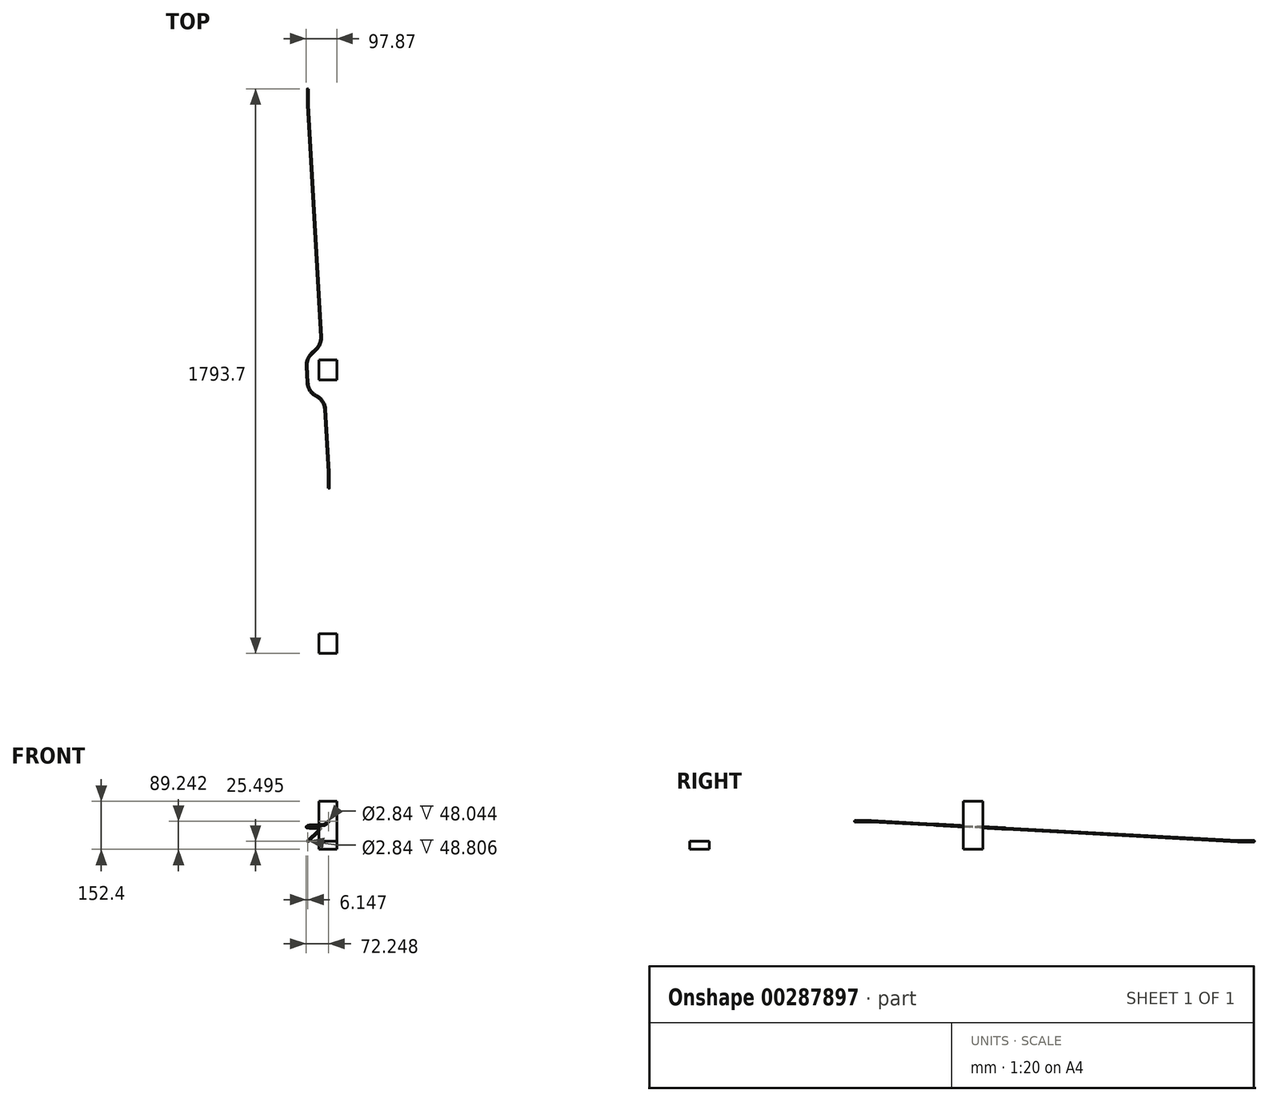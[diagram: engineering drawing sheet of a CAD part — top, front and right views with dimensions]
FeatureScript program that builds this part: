
annotation { "Feature Type Name" : "Feature", "Feature Type Description" : "" }
export const myFeature = defineFeature(function(context is Context, id is Id, definition is map)
    precondition{}
    {
        {
            var Q0;
            Q0=qCreatedBy(makeId("Top.planeOp"),FACE);
            var sketch = newSketch(context, id + "F0", { "sketchPlane" : qUnion([Q0])});
            skLineSegment(sketch, "E0", {"start": v(0, 0) * mm, "end": v(2.87, 0) * mm});
            skLineSegment(sketch, "E1", {"start": v(2.87, 0) * mm, "end": v(2.87, 58) * mm});
            skLineSegment(sketch, "E2", {"start": v(2.87, 58) * mm, "end": v(28.27, 58) * mm});
            skLineSegment(sketch, "E3", {"start": v(0, 0) * mm, "end": v(-63.23, 0) * mm});
            skLineSegment(sketch, "E4", {"start": v(-63.23, 0) * mm, "end": v(-63.23, 1327.37) * mm});
            skLineSegment(sketch, "E5", {"start": v(-63.23, 1327.37) * mm, "end": v(-37.83, 1327.37) * mm});
            skSolve(sketch);
        }
        {
            var Q0;
            Q0=sQuery(id+"F0.wireOp",EDGE,"E5");
            cPlane(context, id + "F1", {"entities" : qUnion([Q0]), "cplaneType" : CPlaneType.LINE_ANGLE, "offset" : 25.4 * mm, "angle" : 0 * degree, "width" : 152.4 * mm, "height" : 152.4 * mm});
        }
        {
            var Q0;
            Q0=sQuery(id+"F0.wireOp",EDGE,"E2");
            cPlane(context, id + "F2", {"entities" : qUnion([Q0]), "cplaneType" : CPlaneType.LINE_ANGLE, "offset" : 25.4 * mm, "angle" : 0 * degree, "width" : 152.4 * mm, "height" : 152.4 * mm});
        }
        {
            var Q0;
            Q0=qCreatedBy(id+"F2.planeOp",FACE);
            var sketch = newSketch(context, id + "F3", { "sketchPlane" : qUnion([Q0])});
            skLineSegment(sketch, "E6", {"start": v(-2.87, 0) * mm, "end": v(-2.87, 861.48) * mm});
            skSolve(sketch);
        }
        {
            var Q0;
            Q0=qCreatedBy(id+"F1.planeOp",FACE);
            var sketch = newSketch(context, id + "F4", { "sketchPlane" : qUnion([Q0])});
            skLineSegment(sketch, "E7", {"start": v(63.23, 0) * mm, "end": v(63.23, 797.74) * mm});
            skSolve(sketch);
        }
        {
            var Q0;
            Q0=sQuery(id+"F4.wireOp",EDGE,"E7");
            cPlane(context, id + "F5", {"entities" : qUnion([Q0]), "cplaneType" : CPlaneType.LINE_ANGLE, "offset" : 25.4 * mm, "angle" : 90 * degree, "width" : 152.4 * mm, "height" : 152.4 * mm});
        }
        {
            var Q0;
            Q0=sQuery(id+"F4.wireOp",EDGE,"E7");
            cPlane(context, id + "F6", {"entities" : qUnion([Q0]), "cplaneType" : CPlaneType.LINE_ANGLE, "offset" : 25.4 * mm, "angle" : 0 * degree, "width" : 152.4 * mm, "height" : 152.4 * mm});
        }
        {
            var Q0;
            Q0=sQuery(id+"F3.wireOp",EDGE,"E6");
            cPlane(context, id + "F7", {"entities" : qUnion([Q0]), "cplaneType" : CPlaneType.LINE_ANGLE, "offset" : 25.4 * mm, "angle" : 0 * degree, "width" : 152.4 * mm, "height" : 152.4 * mm});
        }
        {
            var Q0;
            Q0=sQuery(id+"F3.wireOp",EDGE,"E6");
            cPlane(context, id + "F8", {"entities" : qUnion([Q0]), "cplaneType" : CPlaneType.LINE_ANGLE, "offset" : 25.4 * mm, "angle" : 90 * degree, "width" : 152.4 * mm, "height" : 152.4 * mm});
        }
        {
            var Q0;
            Q0=qCreatedBy(id+"F8.planeOp",FACE);
            var sketch = newSketch(context, id + "F9", { "sketchPlane" : qUnion([Q0])});
            skCircle(sketch, "E8", {"center": v(-2.87, 861.48) * mm, "radius": 2.18 * mm});
            skSolve(sketch);
        }
        {
            var Q0;
            Q0=qCreatedBy(id+"F5.planeOp",FACE);
            var sketch = newSketch(context, id + "F10", { "sketchPlane" : qUnion([Q0])});
            skCircle(sketch, "E9", {"center": v(63.23, 797.74) * mm, "radius": 2.18 * mm});
            skSolve(sketch);
        }
        {
            var Q0;
            Q0=qCreatedBy(id+"F6.planeOp",FACE);
            var sketch = newSketch(context, id + "F11", { "sketchPlane" : qUnion([Q0])});
            skLineSegment(sketch, "E10", {"start": v(1327.37, 797.74) * mm, "end": v(1276.57, 797.74) * mm});
            skSolve(sketch);
        }
        {
            var Q0;
            Q0=qCreatedBy(id+"F7.planeOp",FACE);
            var sketch = newSketch(context, id + "F12", { "sketchPlane" : qUnion([Q0])});
            skLineSegment(sketch, "E11", {"start": v(58, 861.48) * mm, "end": v(108.8, 861.48) * mm});
            skSolve(sketch);
        }
        {
            var Q0;
            Q0=sQuery(id+"F12.wireOp",VERTEX,"E11.start");
            var Q1;
            Q1=sQuery(id+"F12.wireOp",VERTEX,"E11.end");
            var Q2;
            Q2=sQuery(id+"F11.wireOp",VERTEX,"E10.end");
            cPlane(context, id + "F13", {"entities" : qUnion([Q0, Q1, Q2]), "cplaneType" : CPlaneType.THREE_POINT, "offset" : 25.4 * mm, "width" : 152.4 * mm, "height" : 152.4 * mm});
        }
        {
            var Q0;
            Q0=qCreatedBy(id+"F13.planeOp",FACE);
            var sketch = newSketch(context, id + "F14", { "sketchPlane" : qUnion([Q0])});
            skLineSegment(sketch, "E12", {"start": v(599.92, -110.8) * mm, "end": v(508.25, -1276.57) * mm});
            skLineSegment(sketch, "E13", {"start": v(600.08, -106.81) * mm, "end": v(600.08, -58) * mm});
            skPoint(sketch, "E14.visualSharp", {"position": v(600.08, -108.8) * mm});
            skArc(sketch, "E14.filletArc", {"start": v(599.92, -110.8) * mm, "mid": v(600.04, -108.8) * mm, "end": v(600.08, -106.81) * mm});
            skSolve(sketch);
        }
        {
            var Q0;
            Q0=sQuery(id+"F14.wireOp",EDGE,"E12");
            var Q1;
            Q1=sQuery(id+"F11.wireOp",EDGE,"E10");
            cPlane(context, id + "F15", {"entities" : qUnion([Q0, Q1]), "cplaneType" : CPlaneType.LINE_ANGLE, "offset" : 25.4 * mm, "angle" : 0 * degree, "width" : 152.4 * mm, "height" : 152.4 * mm});
        }
        {
            var Q0;
            Q0=qCreatedBy(id+"F15.planeOp",FACE);
            var sketch = newSketch(context, id + "F16", { "sketchPlane" : qUnion([Q0])});
            skLineSegment(sketch, "E15", {"start": v(508.25, 1327.37) * mm, "end": v(508.25, 1278.56) * mm});
            skLineSegment(sketch, "E16", {"start": v(508.4, 1274.58) * mm, "end": v(599.92, 110.8) * mm});
            skPoint(sketch, "E17.visualSharp", {"position": v(508.25, 1276.57) * mm});
            skArc(sketch, "E17.filletArc", {"start": v(508.25, 1278.56) * mm, "mid": v(508.29, 1276.57) * mm, "end": v(508.4, 1274.58) * mm});
            skSolve(sketch);
        }
        {
            var Q0;
            Q0=makeQuery(id+"F10.imprint","IMPRINT",FACE,{"disambiguationData":[TD([[makeQuery(id+"F10.imprint","IMPRINT",EDGE,{"derivedFrom":sQuery(id+"F10.wireOp",EDGE,"E9")}),1.0]])]});
            var Q1;
            Q1=sQuery(id+"F16.wireOp",EDGE,"E15");
            var Q2;
            Q2=sQuery(id+"F16.wireOp",EDGE,"E17.filletArc");
            var Q3;
            Q3=sQuery(id+"F16.wireOp",EDGE,"E16");
            var Q4;
            Q4=sQuery(id+"F14.wireOp",EDGE,"E14.filletArc");
            var Q5;
            Q5=sQuery(id+"F14.wireOp",EDGE,"E13");
            sweep(context, id + "F17", {"profiles" : qUnion([Q0]), "path" : qUnion([Q1, Q2, Q3, Q4, Q5])});
        }
        {
            var Q0;
            Q0=makeQuery(id+"F17.opSweep","CAP_FACE",FACE,{"disambiguationData":[OSD([sQuery(id+"F10.wireOp",EDGE,"E9"),sQuery(id+"F14.wireOp",VERTEX,"E13.end")])],"isStart":false});
            shell(context, id + "F18", {"entities" : qUnion([Q0]), "thickness" : 0.76 * mm});
        }
        {
            var Q0;
            Q0=qCreatedBy(makeId("Top.planeOp"),FACE);
            var sketch = newSketch(context, id + "F19", { "sketchPlane" : qUnion([Q0])});
            skLineSegment(sketch, "E18", {"start": v(0, 0) * mm, "end": v(-27.9, 0) * mm});
            skLineSegment(sketch, "E19", {"start": v(-27.9, 0) * mm, "end": v(-27.9, -466.33) * mm});
            skLineSegment(sketch, "E20", {"start": v(-27.9, -466.33) * mm, "end": v(-2.5, -466.33) * mm});
            skLineSegment(sketch, "E21", {"start": v(0, 0) * mm, "end": v(28.49, 0) * mm});
            skLineSegment(sketch, "E22", {"start": v(28.49, 0) * mm, "end": v(28.49, -403.6) * mm});
            skLineSegment(sketch, "E23", {"start": v(28.49, -403.6) * mm, "end": v(53.89, -403.6) * mm});
            skSolve(sketch);
        }
        {
            var Q0;
            Q0=sQuery(id+"F19.wireOp",EDGE,"E20");
            cPlane(context, id + "F20", {"entities" : qUnion([Q0]), "cplaneType" : CPlaneType.LINE_ANGLE, "offset" : 25.4 * mm, "angle" : 0 * degree, "width" : 152.4 * mm, "height" : 152.4 * mm});
        }
        {
            var Q0;
            Q0=sQuery(id+"F19.wireOp",EDGE,"E23");
            cPlane(context, id + "F21", {"entities" : qUnion([Q0]), "cplaneType" : CPlaneType.LINE_ANGLE, "offset" : 25.4 * mm, "angle" : 0 * degree, "width" : 152.4 * mm, "height" : 152.4 * mm});
        }
        {
            var Q0;
            Q0=qCreatedBy(id+"F20.planeOp",FACE);
            var sketch = newSketch(context, id + "F22", { "sketchPlane" : qUnion([Q0])});
            skLineSegment(sketch, "E24", {"start": v(27.9, 0) * mm, "end": v(27.9, 772.24) * mm});
            skLineSegment(sketch, "E25", {"start": v(27.9, 772.24) * mm, "end": v(2.5, 772.24) * mm});
            skSolve(sketch);
        }
        {
            var Q0;
            Q0=qCreatedBy(id+"F21.planeOp",FACE);
            var sketch = newSketch(context, id + "F23", { "sketchPlane" : qUnion([Q0])});
            skLineSegment(sketch, "E26", {"start": v(-28.49, 0) * mm, "end": v(-28.49, 772.24) * mm});
            skSolve(sketch);
        }
        {
            var Q0;
            Q0=sQuery(id+"F22.wireOp",EDGE,"E25");
            cPlane(context, id + "F24", {"entities" : qUnion([Q0]), "cplaneType" : CPlaneType.LINE_ANGLE, "offset" : 25.4 * mm, "angle" : 90 * degree, "width" : 152.4 * mm, "height" : 152.4 * mm});
        }
        {
            var Q0;
            Q0=qCreatedBy(id+"F24.planeOp",FACE);
            var sketch = newSketch(context, id + "F25", { "sketchPlane" : qUnion([Q0])});
            skLineSegment(sketch, "E27.bottom", {"start": v(-27.9, -466.33) * mm, "end": v(28.49, -466.33) * mm});
            skLineSegment(sketch, "E27.top", {"start": v(-27.9, -403.6) * mm, "end": v(28.49, -403.6) * mm});
            skLineSegment(sketch, "E27.left", {"start": v(-27.9, -466.33) * mm, "end": v(-27.9, -403.6) * mm});
            skLineSegment(sketch, "E27.right", {"start": v(28.49, -466.33) * mm, "end": v(28.49, -403.6) * mm});
            skSolve(sketch);
        }
        {
            var Q0;
            Q0=qSketchRegion(id+"F25",true);
            extrude(context, id + "F26", {"entities" : qUnion([Q0]), "depth" : 25.4 * mm});
        }
        {
            var Q0;
            Q0=qCreatedBy(makeId("Top.planeOp"),FACE);
            var sketch = newSketch(context, id + "F27", { "sketchPlane" : qUnion([Q0])});
            skLineSegment(sketch, "E28", {"start": v(0, 0) * mm, "end": v(28.44, 0) * mm});
            skLineSegment(sketch, "E29", {"start": v(28.44, 0) * mm, "end": v(28.44, 465.82) * mm});
            skLineSegment(sketch, "E30", {"start": v(28.44, 465.82) * mm, "end": v(3.04, 465.82) * mm});
            skLineSegment(sketch, "E31", {"start": v(0, 0) * mm, "end": v(-27.96, 0) * mm});
            skLineSegment(sketch, "E32", {"start": v(-27.96, 0) * mm, "end": v(-27.96, 403.08) * mm});
            skLineSegment(sketch, "E33", {"start": v(-27.96, 403.08) * mm, "end": v(-53.36, 403.08) * mm});
            skSolve(sketch);
        }
        {
            var Q0;
            Q0=sQuery(id+"F27.wireOp",EDGE,"E30");
            cPlane(context, id + "F28", {"entities" : qUnion([Q0]), "cplaneType" : CPlaneType.LINE_ANGLE, "offset" : 25.4 * mm, "angle" : 0 * degree, "width" : 152.4 * mm, "height" : 152.4 * mm});
        }
        {
            var Q0;
            Q0=sQuery(id+"F27.wireOp",EDGE,"E33");
            cPlane(context, id + "F29", {"entities" : qUnion([Q0]), "cplaneType" : CPlaneType.LINE_ANGLE, "offset" : 25.4 * mm, "angle" : 0 * degree, "width" : 152.4 * mm, "height" : 152.4 * mm});
        }
        {
            var Q0;
            Q0=qCreatedBy(id+"F28.planeOp",FACE);
            var sketch = newSketch(context, id + "F30", { "sketchPlane" : qUnion([Q0])});
            skLineSegment(sketch, "E34", {"start": v(28.44, 0) * mm, "end": v(28.44, 772.24) * mm});
            skLineSegment(sketch, "E35", {"start": v(28.44, 772.24) * mm, "end": v(3.04, 772.24) * mm});
            skSolve(sketch);
        }
        {
            var Q0;
            Q0=qCreatedBy(id+"F29.planeOp",FACE);
            var sketch = newSketch(context, id + "F31", { "sketchPlane" : qUnion([Q0])});
            skLineSegment(sketch, "E36", {"start": v(-27.96, 0) * mm, "end": v(-27.96, 772.24) * mm});
            skSolve(sketch);
        }
        {
            var Q0;
            Q0=sQuery(id+"F30.wireOp",EDGE,"E35");
            cPlane(context, id + "F32", {"entities" : qUnion([Q0]), "cplaneType" : CPlaneType.LINE_ANGLE, "offset" : 25.4 * mm, "angle" : 90 * degree, "width" : 152.4 * mm, "height" : 152.4 * mm});
        }
        {
            var Q0;
            Q0=qCreatedBy(id+"F32.planeOp",FACE);
            var sketch = newSketch(context, id + "F33", { "sketchPlane" : qUnion([Q0])});
            skLineSegment(sketch, "E37.bottom", {"start": v(28.44, 465.82) * mm, "end": v(-27.96, 465.82) * mm});
            skLineSegment(sketch, "E37.top", {"start": v(28.44, 403.08) * mm, "end": v(-27.96, 403.08) * mm});
            skLineSegment(sketch, "E37.left", {"start": v(28.44, 465.82) * mm, "end": v(28.44, 403.08) * mm});
            skLineSegment(sketch, "E37.right", {"start": v(-27.96, 465.82) * mm, "end": v(-27.96, 403.08) * mm});
            skSolve(sketch);
        }
        {
            var Q0;
            Q0=qSketchRegion(id+"F33",true);
            extrude(context, id + "F34", {"entities" : qUnion([Q0]), "depth" : 152.4 * mm});
        }
        {
            var Q0;
            Q0=makeQuery(id+"F17.opSweep","SWEPT_BODY",BODY,{"disambiguationData":[OSD([sQuery(id+"F10.wireOp",EDGE,"E9"),sQuery(id+"F14.wireOp",EDGE,"E13")])]});
            deleteBodies(context, id + "F35", {"entities" : qUnion([Q0])});
        }
        {
            var Q0;
            Q0=sQuery(id+"F16.wireOp",EDGE,"E16");
            cPlane(context, id + "F36", {"entities" : qUnion([Q0]), "cplaneType" : CPlaneType.LINE_ANGLE, "offset" : 25.4 * mm, "angle" : 0 * degree, "width" : 152.4 * mm, "height" : 152.4 * mm});
        }
        {
            var Q0;
            Q0=qCreatedBy(id+"F36.planeOp",FACE);
            var sketch = newSketch(context, id + "F37", { "sketchPlane" : qUnion([Q0])});
            skLineSegment(sketch, "E38", {"start": v(-10.14, -291.91) * mm, "end": v(-20.18, -469.43) * mm});
            skLineSegment(sketch, "E39", {"start": v(-20.18, -469.43) * mm, "end": v(-51.7, -438.97) * mm});
            skLineSegment(sketch, "E40", {"start": v(-67.11, -399.58) * mm, "end": v(-64.14, -346.93) * mm});
            skLineSegment(sketch, "E41", {"start": v(-35.35, -303.98) * mm, "end": v(-10.14, -291.91) * mm});
            skPoint(sketch, "E42.visualSharp", {"position": v(-62.44, -316.94) * mm});
            skArc(sketch, "E42.filletArc", {"start": v(-35.35, -303.98) * mm, "mid": v(-55.62, -321.52) * mm, "end": v(-64.14, -346.93) * mm});
            skPoint(sketch, "E43.visualSharp", {"position": v(-68.42, -422.8) * mm});
            skArc(sketch, "E43.filletArc", {"start": v(-67.11, -399.58) * mm, "mid": v(-63.7, -420.96) * mm, "end": v(-51.7, -438.97) * mm});
            skLineSegment(sketch, "E44", {"start": v(-64.14, -346.93) * mm, "end": v(-13.42, -349.8) * mm});
            skLineSegment(sketch, "E45", {"start": v(-10.14, -291.91) * mm, "end": v(2.76, -63.68) * mm});
            skSolve(sketch);
        }
        {
            var Q0;
            Q0=sQuery(id+"F37.wireOp",EDGE,"E41");
            var Q1;
            Q1=sQuery(id+"F37.wireOp",EDGE,"E45");
            cPlane(context, id + "F38", {"entities" : qUnion([Q0, Q1]), "cplaneType" : CPlaneType.LINE_ANGLE, "offset" : 25.4 * mm, "angle" : 0 * degree, "width" : 152.4 * mm, "height" : 152.4 * mm});
        }
        {
            var Q0;
            Q0=qCreatedBy(id+"F38.planeOp",FACE);
            var sketch = newSketch(context, id + "F39", { "sketchPlane" : qUnion([Q0])});
            skLineSegment(sketch, "E46", {"start": v(-8.45, -261.98) * mm, "end": v(2.76, -63.68) * mm});
            skPoint(sketch, "E47.visualSharp", {"position": v(-10.14, -291.91) * mm});
            skArc(sketch, "E47.filletArc", {"start": v(-35.35, -303.98) * mm, "mid": v(-16.4, -286.5) * mm, "end": v(-8.45, -261.98) * mm});
            skSolve(sketch);
        }
        {
            var Q0;
            Q0=sQuery(id+"F37.wireOp",EDGE,"E39");
            var Q1;
            Q1=sQuery(id+"F16.wireOp",EDGE,"E16");
            cPlane(context, id + "F40", {"entities" : qUnion([Q0, Q1]), "cplaneType" : CPlaneType.LINE_ANGLE, "offset" : 25.4 * mm, "angle" : 0 * degree, "width" : 152.4 * mm, "height" : 152.4 * mm});
        }
        {
            var Q0;
            Q0=qCreatedBy(id+"F40.planeOp",FACE);
            var sketch = newSketch(context, id + "F41", { "sketchPlane" : qUnion([Q0])});
            skLineSegment(sketch, "E48", {"start": v(-51.7, 438.97) * mm, "end": v(-36.9, 453.26) * mm});
            skLineSegment(sketch, "E49", {"start": v(-21.5, 492.66) * mm, "end": v(-63.12, 1229.2) * mm});
            skPoint(sketch, "E50.visualSharp", {"position": v(-20.18, 469.43) * mm});
            skArc(sketch, "E50.filletArc", {"start": v(-36.9, 453.26) * mm, "mid": v(-24.9, 471.28) * mm, "end": v(-21.5, 492.66) * mm});
            skSolve(sketch);
        }
        {
            var Q0;
            Q0=makeQuery(id+"F9.imprint","IMPRINT",FACE,{"disambiguationData":[TD([[makeQuery(id+"F9.imprint","IMPRINT",EDGE,{"derivedFrom":sQuery(id+"F9.wireOp",EDGE,"E8")}),1.0]])]});
            var Q1;
            Q1=sQuery(id+"F14.wireOp",EDGE,"E13");
            var Q2;
            Q2=sQuery(id+"F14.wireOp",EDGE,"E14.filletArc");
            var Q3;
            Q3=sQuery(id+"F39.wireOp",EDGE,"E46");
            var Q4;
            Q4=sQuery(id+"F39.wireOp",EDGE,"E47.filletArc");
            var Q5;
            Q5=sQuery(id+"F37.wireOp",EDGE,"E42.filletArc");
            var Q6;
            Q6=sQuery(id+"F37.wireOp",EDGE,"E40");
            var Q7;
            Q7=sQuery(id+"F37.wireOp",EDGE,"E43.filletArc");
            var Q8;
            Q8=sQuery(id+"F41.wireOp",EDGE,"E48");
            var Q9;
            Q9=sQuery(id+"F41.wireOp",EDGE,"E50.filletArc");
            var Q10;
            Q10=sQuery(id+"F41.wireOp",EDGE,"E49");
            var Q11;
            Q11=sQuery(id+"F16.wireOp",EDGE,"E17.filletArc");
            var Q12;
            Q12=sQuery(id+"F16.wireOp",EDGE,"E15");
            sweep(context, id + "F42", {"profiles" : qUnion([Q0]), "path" : qUnion([Q1, Q2, Q3, Q4, Q5, Q6, Q7, Q8, Q9, Q10, Q11, Q12])});
        }
        {
            var Q0;
            Q0=makeQuery(id+"F42.opSweep","CAP_FACE",FACE,{"disambiguationData":[OSD([sQuery(id+"F9.wireOp",EDGE,"E8"),sQuery(id+"F16.wireOp",VERTEX,"E15.start")])],"isStart":false});
            shell(context, id + "F43", {"entities" : qUnion([Q0]), "thickness" : 0.76 * mm});
        }
        {
            var Q0;
            Q0=makeQuery(id+"F34.opExtrude","SWEPT_BODY",BODY,{"disambiguationData":[OSD([sQuery(id+"F33.wireOp",EDGE,"E37.bottom"),sQuery(id+"F33.wireOp",EDGE,"E37.top"),sQuery(id+"F33.wireOp",EDGE,"E37.left"),sQuery(id+"F33.wireOp",EDGE,"E37.right")])]});
            transform(context, id + "F44", {"entities" : qUnion([Q0]), "transformType" : TransformType.TRANSLATION_3D, "dx" : 0 * mm, "dy" : 0 * mm, "dz" : 0 * mm, "makeCopy" : true});
        }
        {
            var Q0;
            Q0=makeQuery(id+"F34.opExtrude","SWEPT_BODY",BODY,{"disambiguationData":[OSD([sQuery(id+"F33.wireOp",EDGE,"E37.bottom"),sQuery(id+"F33.wireOp",EDGE,"E37.top"),sQuery(id+"F33.wireOp",EDGE,"E37.left"),sQuery(id+"F33.wireOp",EDGE,"E37.right")])]});
            transform(context, id + "F45", {"entities" : qUnion([Q0]), "transformType" : TransformType.TRANSLATION_3D, "dx" : 0 * mm, "dy" : 0 * mm, "dz" : 0 * mm, "makeCopy" : true});
        }
    });
